# Revit family: PD4 FP types Sans hôte
name_source: partatom
category: Dispositifs d'éclairage
units: mm (PartAtom-declared; Revit-internal decimal feet)

## family parameters
Basée sur le plan de construction = Oui
Conserver l'orientation des annotations = Non
Cote de connecteur circulaire = Utiliser le diamètre
Couper avec des vides une fois chargée = Non
Partagée = Non
Point de calcul de pièce = Non
Toujours verticalement = Oui
Type d'élément = Normal

## types (28) — shared parameters
Classe = II
Code d'assemblage = D5010200
Fabricant = B.E.G.
Hauteur de montage max = 350 cm
Image du type = 360°.jpg
Marque = LUXOMAT
Mode de pose = Faux Plafond
URL = https://www.beg-luxomat.com
zero-valued in all types: Elévation par défaut

## per-type parameters (varying)
| type | Alimentation | Charge Cos ɸ =0.5 | Charge Cos ɸ =1 | Charge LED | Commentaires du type | Consommation | IP | Modèle | Relais | Référence | Température ambiante | Type de Sortie |
| 01- PD4 FP Générique | 110-240 V AC |  |  |  | DET.PRES.360°/Ø24M FAUX PLAFOND |  | 20 | PD4 FP |  |  | -25°C à +50°C |  |
| 02- PD4N 1C FP réf 92149 | 110-240 V AC | 1150 VA | 2300 W | 300 W | DET.MOUV.1 CONTACT.360°/Ø24M FAUX PLAFOND | 0,25 W | 23 | PD4N 1C FP | 10 A | 92149 | -25°C à +50°C | TOR |
| 03- PD4 M 1C FP réf 92585 | 110-240 V AC | 1150 VA | 2300 W | 300 W | DET.PRES.MAITRE.1 CONTACT.360°/Ø24M FAUX PLAFOND | 0,45 W | 20 | PD4 M 1C FP | 10 A | 92585 | -25°C à +50°C | TOR |
| 04- PD4 M 2C FP réf 92148 | 110-240 V AC | 1150 VA | 2300 W | 300 W | DET.PRES.MAITRE.2 CONTACTS.360°/Ø24M FAUX PLAFOND | 0,47 W | 20 | PD4 M 2C FP | 10 A / 3 A | 92148 | -25°C à +50°C | TOR + CVC |
| 05- PD4 M 2C DUO FP réf 92251 | 110-240 V AC | 1150 VA | 2300 W | 300 W | DET.PRES.MAITRE.DUO.2 CONTACTS.360°/Ø24M FAUX PLAFOND | 0,47 W | 20 | PD4 M 2C DUO FP | 10 A | 92251 | -25°C à +50°C | 2  TOR (1er jour/2ème jour) |
| 06- PD4 M 3C TRIO FP réf 92745 | 110-240 V AC | 1500 VA | 3000 W | 300 W | DET.PRES.MAITRE.TRIO.3 CONTACTS.360°/Ø24M FAUX PLAFOND | 0,58 W | 20 | PD4 M 3C TRIO FP | 16 A | 92745 | -25°C à +50°C | 3  TOR (1er jour/2ème jour + Tableau ou CVC) |
| 13- PD4 M DIM FP réf 92247 | 110-240 V AC | 1150 VA | 2300 W | 300 W | DET.PRES.MAITRE.DIM(1-10V).360°/Ø24M FAUX PLAFOND | 0,50 W | 20 | PD4 M DIM FP | 10 A | 92247 | -25°C à +50°C | DIM (50 ballasts maxi) |
| 14- PD4 M DIM CVC FP réf 92507 | 110-240 V AC | 1150 VA | 2300 W | 300 W | DET.PRES.MAITRE.DIM(1-10V) + CVC 3A.360°/Ø24M FAUX PLAFOND | 0,50 W | 20 | PD4 M DIM CVC FP | 10 A / 3 A | 92507 | -25°C à +50°C | DIM (50 ballasts maxi) + CVC |
| 15- PD4 M DIM CVC 16A FP réf 92547 | 110-240 V AC | 1150 VA / 1500 VA | 2300 W / 3000 W | 300 W / 300 W | DET.PRES.MAITRE.DIM(1-10V) + CVC 16A.360°/Ø24M FAUX PLAFOND | 0,54 W | 20 | PD4 M DIM CVC 16A FP | 10 A / 16 A | 92547 | -25°C à +50°C | DIM (50 ballasts maxi) + CVC |
| 16- PD4 M DUO DIM FP réf 92272 | 110-240 V AC | 1150 VA | 2300 W | 300 W | DET.PRES.MAITRE.DUO.2 DIM(1-10V).360°/Ø24M FAUX PLAFOND | 0,50 W | 20 | PD4 M DUO DIM FP | 10 A | 92272 | -25°C à +50°C | 2 DIM (25 ballasts maxi-1er jour/2ème jour) |
| 17- PD4 M TRIO DIM FP réf 92735 | 110-240 V AC | 1500 VA | 3000 W | 300 W | DET.PRES.MAITRE.TRIO.2 DIM(1-10V) + TOR.360°/Ø24M FAUX PLAFOND | 0,78 W | 20 | PD4 M TRIO DIM FP | 16 A | 92735 | -25°C à +50°C | 2 DIM (25 ballasts maxi-1er jour/2ème jour) + TOR (Tableau ou CVC) |
| 07- PD4N M DACO FP réf 93460 | 110-240 V AC | 0 | 0 | 0 | DET.PRES.MAITRE.DALI 2.360°/Ø24M FAUX PLAFOND | 2 W | 20 | PD4N M DACO FP | 0 | 93460 | -25°C à +50°C | DALI 2  (40 drivers maxi) |
| 08- PD4N M DACO 1C FP réf 93463 | 110-240 V AC | 1150 VA | 2300 W | 300 W | DET.PRES.MAITRE.DALI 2 + CONTACT NO.360°/Ø24M FAUX PLAFOND | 2 W | 20 | PD4N M DACO 1C FP | 10 A | 93463 | -25°C à +50°C | DALI 2 (40 drivers maxi) + Contact NO |
| 09- PD4 M DUO DALI/DSI FP réf 92276 | 110-240 V AC | 0 | 0 | 0 | DET.PRES.MAITRE.DUO.2 DALI/DSI.360°/Ø24M FAUX PLAFOND | 0,50 W | 20 | PD4 M DUO DALI/DSI FP | 0 | 92276 | -25°C à +50°C | 2 DALI (25 ballasts maxi-1er jour/2ème jour) |
| 10- PD4 M TRIO 2DALI/DSI 1C FP réf 92756 | 110-240 V AC | 1500 VA | 3000 W | 300 W | DET.PRES.MAITRE.TRIO.2 DALI/DSI + TOR.360°/Ø24M FAUX PLAFOND | 0,78 W | 20 | PD4 M TRIO 2 DALI/DSI 1C FP | 16 A | 92756 | -25°C à +50°C | 2 DALI (25 ballasts maxi-1er jour/2ème jour) + TOR (Tableau ou CVC) |
| 11- PD4 M DAA4G FP réf 92591 | 110-240 V AC | 1150 VA | 2300 W | 300 W | DET.PRES.MAITRE.DALI ADRESSABLE AUTONOME + TOR.360°/Ø24M FAUX PLAFOND | 0.4 W | 20 | PD4 M DAA4G FP | 10 A | 92591 | -25°C à +50°C | DALI Adressable Autonome (64 ballasts maxi) + TOR |
| 28- PD4N LTMS RR FP réf 92709 | 11-48 V DC | 0 | 0 | 0 | DET.PRES.11-48V.1 CONTACT.RR.360°/Ø24M FAUX PLAFOND | > 1 W | 20 | PD4N LTMS RR FP | 100 mA | 92709 | 0°C à +50°C | Reed Relais |
| 23- PD4N KNX ST FP réf 93384 | 24 V DC par bus KNX | 0 | 0 | 0 | DET.PRES.KNX.VERSION STANDARD.360°/Ø24M FAUX PLAFOND | 12 mA | 20 | PD4N KNX ST FP | 0 | 93384 | -5°C à +45°C | KNX - 1 sortie Eclairage TOR ou GRADATION / 3 sorties Présence |
| 24- PD4N KNX DX FP réf 93386 | 24 V DC par bus KNX | 0 | 0 | 0 | DET.PRES.KNX.VERSION DELUXE.360°/Ø24M FAUX PLAFOND | 12 mA | 20 | PD4N KNX DX FP | 0 | 93386 | -5°C à +45°C | KNX - 1 sortie Eclairage TOR ou GRADATION / 3 sorties Présence / Capteur de température et bruit |
| 27- PD4N LON FP réf 92831 | 24 V DC par bus LON | 0 | 0 | 0 | DET.PRES.LON.360°/Ø24M FAUX PLAFOND | 12 mA | 20 | PD4N LON FP | 0 | 92831 | -5°C à +45°C | LON |
| 22- PD4N BMS DALI 2 FP réf 93546 | 10-22V DC par bus DALI | 0 | 0 | 0 | MULTI.CAPTEUR.PRES.BMS.DALI 2.360°/Ø24M FAUX PLAFOND | 7 mA | 20 | PD4N BMS DALI 2 FP | 0 | 93546 | -25°C à +50°C | DALI 2 adressable - BMS |
| 18- PD4 S FP réf 92254 | 110-240 V AC | 0 | 0 | 0 | DET.PRES.ESCLAVE.360°/Ø24M FAUX PLAFOND | 0,25 W | 20 | PD4 S FP | 0 | 92254 | -25°C à +50°C | Esclave |
| 19- PD4 S DAA4G FP réf 92721 | 22 V DC par bus DALI | 0 | 0 | 0 | DET.PRES.ESCLAVE.DALI.360°/Ø24M FAUX PLAFOND | 7 mA | 20 | PD4 S DAA4G FP | 0 | 92721 | -25°C à +50°C | DALI Esclave |
| 12- PD4 M HCL2 FP réf 93484 | 110-240 V AC | 1150 VA | 2300 W | 300 W | DET.PRES.MAITRE.DALI HCL ADRESSABLE AUTONOME + TOR.360°/Ø24M FAUX PLAFOND | 0.4 W | 20 | PD4 M HCL2 FP | 10 A | 93484 | -25°C à +50°C | DALI HCL Adressable Autonome (64 ballasts maxi) + TOR |
| 20- PD4N DALILINK FP réf 93377 | 16V DC par bus DALI | 0 | 0 | 0 | MULTI.CAPTEUR.PRES.DALILINK.360°/Ø24M FAUX PLAFOND | 7 mA | 20 | PD4N DALILINK FP | 0 | 93377 | -25°C à +55°C | DALILINK |
| 21- PD4N DALISYS FP réf 93340 | 10-22V DC par bus DALI | 0 | 0 | 0 | MULTI.CAPTEUR.PRES.DALISYS.360°/Ø24M FAUX PLAFOND | 7 mA | 20 | PD4N DALISYS FP | 0 | 93340 | -25°C à +55°C | DALI adressable |
| 25- PD4N KNXs ST FP réf 93514 | 24 V DC par bus KNX | 0 | 0 | 0 | DET.PRES.KNX Sécure.VERSION STANDARD.360°/Ø24M FAUX PLAFOND | 12 mA | 20 | PD4N KNXs ST FP | 0 | 93514 | -5°C à +45°C | KNX Sécure - 1 sortie Eclairage TOR ou GRADATION / 3 sorties Présence / HCL |
| 26- PD4N KNXs DX FP réf 93516 | 24 V DC par bus KNX | 0 | 0 | 0 | DET.PRES.KNX Sécure.VERSION DELUXE.360°/Ø24M FAUX PLAFOND | 12 mA | 20 | PD4N KNXs DX FP | 0 | 93516 | -5°C à +45°C | KNX Sécure - 1 sortie Eclairage TOR ou GRADATION / 3 sorties Présence / Capteur de température et bruit / HCL |
